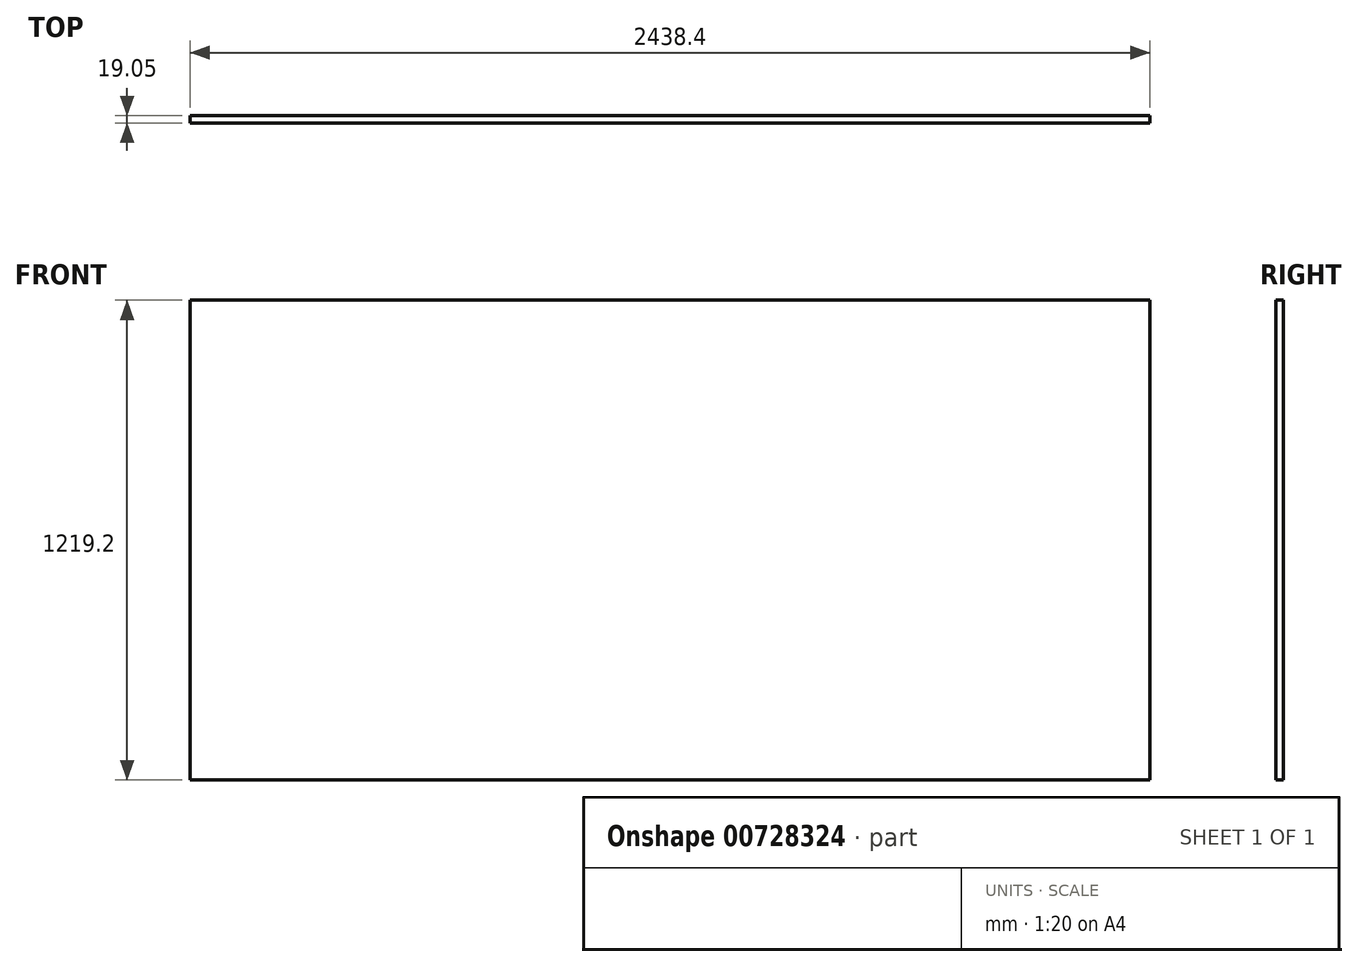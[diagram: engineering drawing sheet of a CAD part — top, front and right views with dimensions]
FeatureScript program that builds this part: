
annotation { "Feature Type Name" : "Feature", "Feature Type Description" : "" }
export const myFeature = defineFeature(function(context is Context, id is Id, definition is map)
    precondition{}
    {
        {
            var Q0;
            Q0=qCreatedBy(makeId("Front.planeOp"),FACE);
            var sketch = newSketch(context, id + "F0", { "sketchPlane" : qUnion([Q0])});
            skLineSegment(sketch, "E0.bottom", {"start": v(1160.51, -401.1) * mm, "end": v(-1277.89, -401.1) * mm});
            skLineSegment(sketch, "E0.top", {"start": v(1160.51, 818.1) * mm, "end": v(-1277.89, 818.1) * mm});
            skLineSegment(sketch, "E0.left", {"start": v(1160.51, -401.1) * mm, "end": v(1160.51, 818.1) * mm});
            skLineSegment(sketch, "E0.right", {"start": v(-1277.89, -401.1) * mm, "end": v(-1277.89, 818.1) * mm});
            skPoint(sketch, "E0.middle", {"position": v(-58.69, 208.5) * mm});
            skSolve(sketch);
        }
        {
            var Q0;
            Q0=qSketchRegion(id+"F0",true);
            extrude(context, id + "F1", {"entities" : qUnion([Q0]), "depth" : 19.05 * mm});
        }
    });
